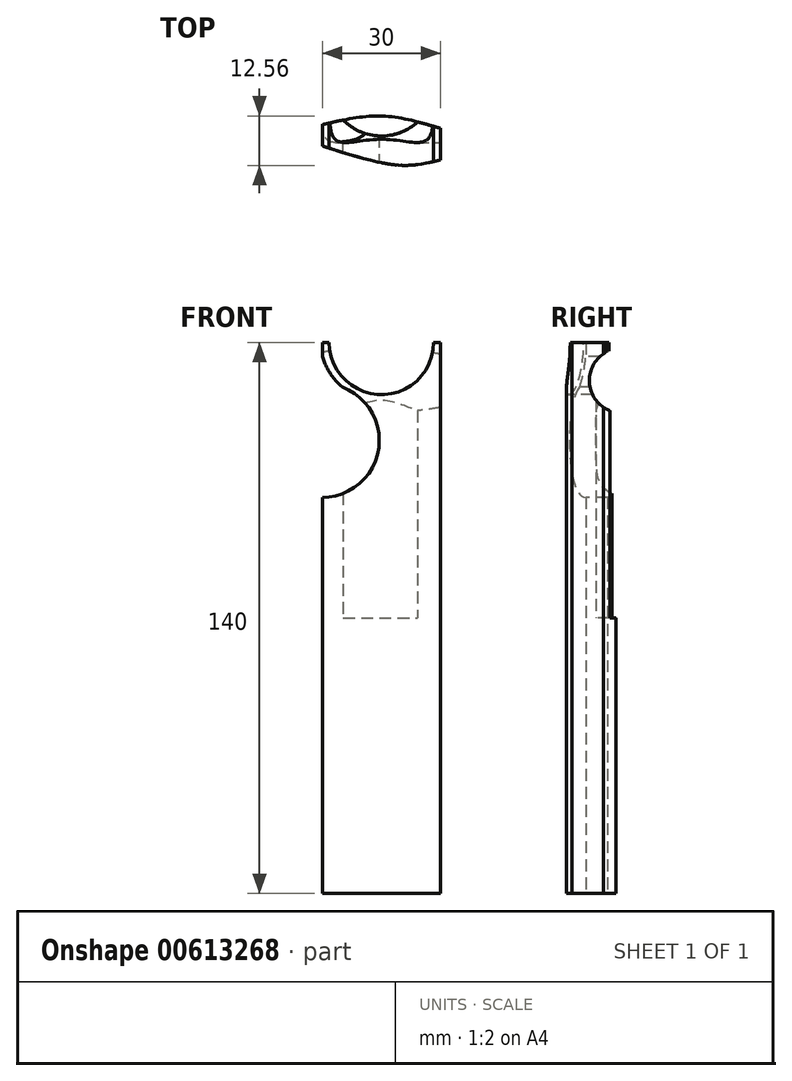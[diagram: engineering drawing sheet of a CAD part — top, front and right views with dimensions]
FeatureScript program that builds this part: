
annotation { "Feature Type Name" : "Feature", "Feature Type Description" : "" }
export const myFeature = defineFeature(function(context is Context, id is Id, definition is map)
    precondition{}
    {
        {
            var Q0;
            Q0=qCreatedBy(makeId("Front.planeOp"),FACE);
            var sketch = newSketch(context, id + "F0", { "sketchPlane" : qUnion([Q0])});
            skLineSegment(sketch, "E0.bottom", {"start": v(15, -70) * mm, "end": v(-15, -70) * mm});
            skLineSegment(sketch, "E0.top", {"start": v(15, 70) * mm, "end": v(-15, 70) * mm});
            skLineSegment(sketch, "E0.left", {"start": v(15, -70) * mm, "end": v(15, 70) * mm});
            skLineSegment(sketch, "E0.right", {"start": v(-15, -70) * mm, "end": v(-15, 70) * mm});
            skPoint(sketch, "E0.middle", {"position": v(0, 0) * mm});
            skSolve(sketch);
        }
        {
            var Q0;
            Q0=makeQuery(id+"F0.imprint","IMPRINT",FACE,{"disambiguationData":[TD([[makeQuery(id+"F0.imprint","IMPRINT",EDGE,{"derivedFrom":sQuery(id+"F0.wireOp",EDGE,"E0.bottom")}),-1.0]])]});
            extrude(context, id + "F1", {"entities" : qUnion([Q0]), "depth" : 30 * mm, "offsetDistance" : 25 * mm});
        }
        {
            var Q0;
            Q0=makeQuery(id+"F1.opExtrude","CAP_FACE",FACE,{"disambiguationData":[OSD([sQuery(id+"F0.wireOp",EDGE,"E0.bottom"),sQuery(id+"F0.wireOp",EDGE,"E0.top"),sQuery(id+"F0.wireOp",EDGE,"E0.left"),sQuery(id+"F0.wireOp",EDGE,"E0.right")])],"isStart":false});
            var sketch = newSketch(context, id + "F2", { "sketchPlane" : qUnion([Q0])});
            skCircle(sketch, "E1", {"center": v(0, 70) * mm, "radius": 13.25 * mm});
            skSolve(sketch);
        }
        {
            var Q0;
            Q0 = qSketchRegion(id + "F2", true);
            extrude(context, id + "F3", {"entities" : qUnion([Q0]), "operationType" : NewBodyOperationType.REMOVE, "oppositeDirection" : true, "depth" : 54.4 * mm, "offsetDistance" : 25 * mm});
        }
        {
            var Q0;
            Q0=makeQuery(id+"F1.opExtrude","CAP_FACE",FACE,{"disambiguationData":[OSD([sQuery(id+"F0.wireOp",EDGE,"E0.bottom"),sQuery(id+"F0.wireOp",EDGE,"E0.top"),sQuery(id+"F0.wireOp",EDGE,"E0.left"),sQuery(id+"F0.wireOp",EDGE,"E0.right")])],"isStart":false});
            var sketch = newSketch(context, id + "F4", { "sketchPlane" : qUnion([Q0])});
            skCircle(sketch, "E2", {"center": v(-15, 45.12) * mm, "radius": 14.45 * mm});
            skSolve(sketch);
        }
        {
            var Q0;
            Q0 = qSketchRegion(id + "F4", true);
            extrude(context, id + "F5", {"entities" : qUnion([Q0]), "operationType" : NewBodyOperationType.REMOVE, "oppositeDirection" : true, "depth" : 128.1 * mm, "offsetDistance" : 25 * mm});
        }
        {
            var Q0;
            Q0=makeQuery(id+"F1.opExtrude","CAP_FACE",FACE,{"disambiguationData":[OSD([sQuery(id+"F0.wireOp",EDGE,"E0.bottom"),sQuery(id+"F0.wireOp",EDGE,"E0.top"),sQuery(id+"F0.wireOp",EDGE,"E0.left"),sQuery(id+"F0.wireOp",EDGE,"E0.right")])],"isStart":false});
            var sketch = newSketch(context, id + "F6", { "sketchPlane" : qUnion([Q0])});
            skArc(sketch, "E3", {"start": v(-15, 66.45) * mm, "mid": v(-13.01, 62.2) * mm, "end": v(-9.94, 58.65) * mm});
            skLineSegment(sketch, "E4", {"start": v(-15, 66.45) * mm, "end": v(-21.47, 59.25) * mm});
            skLineSegment(sketch, "E5", {"start": v(-21.47, 59.25) * mm, "end": v(-15, 55.85) * mm});
            skLineSegment(sketch, "E6", {"start": v(-15, 55.85) * mm, "end": v(-9.94, 58.65) * mm});
            skSolve(sketch);
        }
        {
            var Q0;
            Q0 = qSketchRegion(id + "F6", true);
            extrude(context, id + "F7", {"entities" : qUnion([Q0]), "operationType" : NewBodyOperationType.REMOVE, "oppositeDirection" : true, "depth" : 70.9 * mm, "offsetDistance" : 25 * mm});
        }
        {
            var Q0;
            Q0=makeQuery(id+"F1.opExtrude","SWEPT_FACE",FACE,{"disambiguationData":[OSD([sQuery(id+"F0.wireOp",EDGE,"E0.bottom")])]});
            var sketch = newSketch(context, id + "F8", { "sketchPlane" : qUnion([Q0])});
            skFitSpline(sketch, "E7", {"points": [v(15, 23.5) * mm, v(4.76, 24.87) * mm, v(-15, 19.98) * mm], "startDerivative": vector(-22.7, 5.69) * mm, "endDerivative": vector(-36.52, -11.78) * mm});
            skPoint(sketch, "E8.1.internal.snap0", {"position": v(-15, 15) * mm});
            skFitSpline(sketch, "E8", {"points": [v(-15, 19.98) * mm, v(-13.45, 15) * mm, v(10.06, 12.23) * mm, v(15, 12.5) * mm], "startDerivative": vector(-2.2, -22.76) * mm, "endDerivative": vector(14.12, 1.38) * mm});
            skLineSegment(sketch, "E9", {"start": v(15, 23.5) * mm, "end": v(15, 12.5) * mm});
            skLineSegment(sketch, "E10", {"start": v(15, 23.5) * mm, "end": v(28.67, 27.31) * mm});
            skLineSegment(sketch, "E11", {"start": v(28.67, 27.31) * mm, "end": v(25.28, 39.5) * mm});
            skLineSegment(sketch, "E12", {"start": v(25.28, 39.5) * mm, "end": v(-18.2, 41.31) * mm});
            skLineSegment(sketch, "E13", {"start": v(-18.2, 41.31) * mm, "end": v(-27.31, 36.96) * mm});
            skLineSegment(sketch, "E14", {"start": v(-27.31, 36.96) * mm, "end": v(-15, 19.98) * mm});
            skSolve(sketch);
        }
        {
            var Q0;
            {var subQ0=sQuery(id+"F8.wireOp",EDGE,"E7");Q0=makeQuery(id+"F8.imprint","IMPRINT",FACE,{"disambiguationData":[TD([[makeQuery(id+"F8.imprint","IMPRINT",EDGE,{"derivedFrom":subQ0}),-1.0]])]});}
            var Q1;
            {var subQ0=sQuery(id+"F8.wireOp",EDGE,"E10");Q1=makeQuery(id+"F8.imprint","IMPRINT",FACE,{"disambiguationData":[TD([[makeQuery(id+"F8.imprint","IMPRINT",EDGE,{"derivedFrom":subQ0}),1.0]])]});}
            extrude(context, id + "F9", {"entities" : qUnion([Q0, Q1]), "operationType" : NewBodyOperationType.REMOVE, "oppositeDirection" : true, "depth" : 175.5 * mm, "offsetDistance" : 25 * mm});
        }
        {
            var Q0;
            Q0=makeQuery(id+"F1.opExtrude","SWEPT_FACE",FACE,{"disambiguationData":[OSD([sQuery(id+"F0.wireOp",EDGE,"E0.bottom")])]});
            var sketch = newSketch(context, id + "F10", { "sketchPlane" : qUnion([Q0])});
            skFitSpline(sketch, "E15", {"points": [v(-14.95, 14.54) * mm, v(0, 12.37) * mm, v(15, 15.5) * mm], "startDerivative": vector(30.03, -7) * mm, "endDerivative": vector(29.87, 8.89) * mm});
            skLineSegment(sketch, "E16", {"start": v(15, 15.5) * mm, "end": v(25.28, 14.4) * mm});
            skLineSegment(sketch, "E17", {"start": v(25.28, 14.4) * mm, "end": v(23.2, -5.27) * mm});
            skLineSegment(sketch, "E18", {"start": v(23.2, -5.27) * mm, "end": v(-17.8, -5.27) * mm});
            skLineSegment(sketch, "E19", {"start": v(-17.8, -5.27) * mm, "end": v(-21.6, 3.8) * mm});
            skLineSegment(sketch, "E20", {"start": v(-21.6, 3.8) * mm, "end": v(-14.95, 14.54) * mm});
            skSolve(sketch);
        }
        {
            var Q0;
            {var subQ3=sQuery(id+"F10.wireOp",EDGE,"E15");Q0=makeQuery(id+"F10.imprint","IMPRINT",FACE,{"disambiguationData":[TD([[makeQuery(id+"F10.imprint","IMPRINT",EDGE,{"derivedFrom":subQ3}),-1.0]])]});}
            var Q1;
            {var subQ1=sQuery(id+"F10.wireOp",EDGE,"E16");Q1=makeQuery(id+"F10.imprint","IMPRINT",FACE,{"disambiguationData":[TD([[makeQuery(id+"F10.imprint","IMPRINT",EDGE,{"derivedFrom":subQ1}),-1.0]])]});}
            extrude(context, id + "F11", {"entities" : qUnion([Q0, Q1]), "operationType" : NewBodyOperationType.REMOVE, "oppositeDirection" : true, "depth" : 153.2 * mm, "offsetDistance" : 25 * mm});
        }
        {
            var Q0;
            Q0=qCreatedBy(makeId("Right.planeOp"),FACE);
            var sketch = newSketch(context, id + "F12", { "sketchPlane" : qUnion([Q0])});
            skCircle(sketch, "E21", {"center": v(-10.87, 60.34) * mm, "radius": 8.21 * mm});
            skSolve(sketch);
        }
        {
            var Q0;
            Q0 = qSketchRegion(id + "F12", true);
            extrude(context, id + "F13", {"entities" : qUnion([Q0]), "operationType" : NewBodyOperationType.REMOVE, "endBound" : BoundingType.SYMMETRIC, "oppositeDirection" : true, "depth" : 66.2 * mm, "offsetDistance" : 25 * mm});
        }
        {
            var Q0;
            Q0=qCreatedBy(makeId("Top.planeOp"),FACE);
            var sketch = newSketch(context, id + "F14", { "sketchPlane" : qUnion([Q0])});
            skCircle(sketch, "E22", {"center": v(0, -3.8) * mm, "radius": 13.64 * mm});
            skSolve(sketch);
        }
        {
            var Q0;
            Q0 = qSketchRegion(id + "F14", true);
            var Q1;
            Q1=makeQuery(id+"F14.imprint","IMPRINT",FACE,{"disambiguationData":[TD([[makeQuery(id+"F14.imprint","IMPRINT",EDGE,{"derivedFrom":sQuery(id+"F14.wireOp",EDGE,"E22")}),1.0]])]});
            extrude(context, id + "F15", {"entities" : qUnion([Q0, Q1]), "operationType" : NewBodyOperationType.REMOVE, "depth" : 73.6 * mm, "offsetDistance" : 25 * mm});
        }
    });
